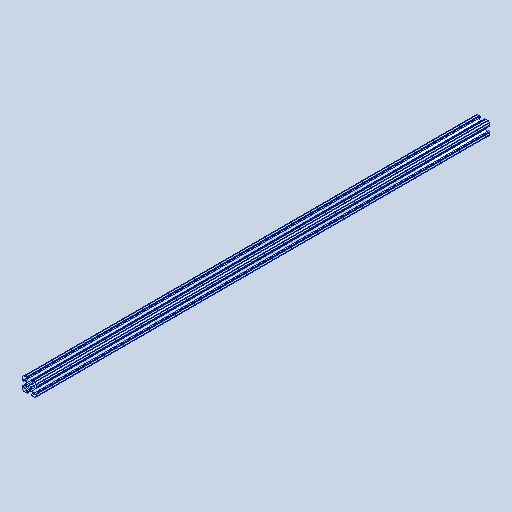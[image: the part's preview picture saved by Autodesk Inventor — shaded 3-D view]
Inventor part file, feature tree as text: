
AUTODESK INVENTOR PART (.ipt)
format: ipt  version: 2023 (Build 270158000, 158)  size: 492,032 bytes
history: native  units: in
note: dims shown in document units (in); Inventor stores cm internally (conversion verified against a paired STEP export)
features: extrude x1, sketch x1, projected_geometry x1, other x1
ambient origin geometry x8: Origin, YZ Plane, XZ Plane, XY Plane, X Axis, Y Axis, Z Axis, Center Point
bodies: Solid1 (feature_tree)
feature tree (4):
  extrude  "Extrusion1"  [1 undecoded]
  sketch  "Sketch1"  dims[d0=22.0in d1=0.0in]
  projected_geometry  "Projected Loop1"
  other  "Boss-Extrude1"
note: 1 required parameter value undecoded (feature->parameter linkage not recoverable at this tier; creation-order binding heuristic only, values carry confidence <= 0.55)
